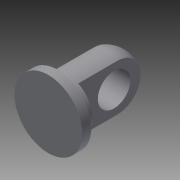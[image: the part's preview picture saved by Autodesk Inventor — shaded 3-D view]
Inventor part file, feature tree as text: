
AUTODESK INVENTOR PART (.ipt)
format: ipt  version: 2013 (Build 170138000, 138)  size: 110,592 bytes
history: native  units: mm
features: extrude x4, sketch x4, fillet x1
ambient origin geometry x8: Origin, YZ Plane, XZ Plane, XY Plane, X Axis, Y Axis, Z Axis, Center Point
bodies: Solid1 (feature_tree)
feature tree (9):
  extrude  "Extrusion1"  Depth=1.4mm TaperAngle=0.0deg
  extrude  "Extrusion2"  Depth=1.4mm TaperAngle=0.0deg
  extrude  "Extrusion3"  Depth=4.5mm
  extrude  "Extrusion4"  Depth=10.0mm TaperAngle=0.0deg
  fillet  "Fillet1"  Radius=4.0mm
  sketch  "Sketch1"  dims[d0=10.4mm d1=1.4mm d2=0.0mm]
  sketch  "Sketch2"  dims[d3=8.0mm d4=1.4mm d5=0.0mm]
  sketch  "Sketch3"  dims[d7=10.0mm d8=0.0mm d9=4.5mm]
  sketch  "Sketch4"  dims[d10=5.0mm d11=10.0mm d12=0.0mm d13=4.0mm]
